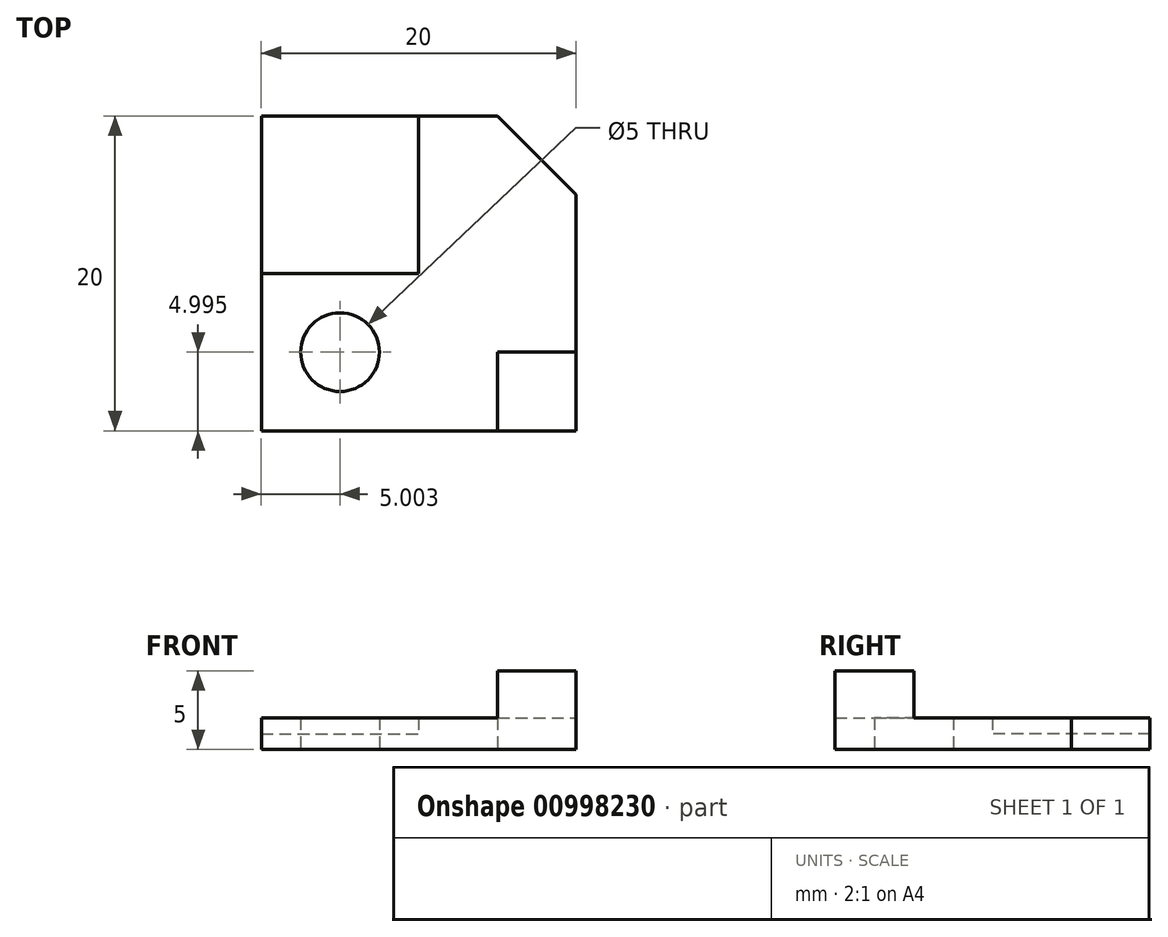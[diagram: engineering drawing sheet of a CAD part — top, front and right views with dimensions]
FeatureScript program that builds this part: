
annotation { "Feature Type Name" : "Feature", "Feature Type Description" : "" }
export const myFeature = defineFeature(function(context is Context, id is Id, definition is map)
    precondition{}
    {
        {
            var Q0;
            Q0=qCreatedBy(makeId("Top.planeOp"),FACE);
            var sketch = newSketch(context, id + "F0", { "sketchPlane" : qUnion([Q0])});
            skLineSegment(sketch, "E0.bottom", {"start": v(-62.42, 35.89) * mm, "end": v(-42.42, 35.89) * mm});
            skLineSegment(sketch, "E0.top", {"start": v(-62.42, 15.89) * mm, "end": v(-42.42, 15.89) * mm});
            skLineSegment(sketch, "E0.left", {"start": v(-62.42, 35.89) * mm, "end": v(-62.42, 15.89) * mm});
            skLineSegment(sketch, "E0.right", {"start": v(-42.42, 35.89) * mm, "end": v(-42.42, 15.89) * mm});
            skPoint(sketch, "E1.oppositeSnap0", {"position": v(-62.42, 25.89) * mm});
            skPoint(sketch, "E1.oppositeSnap1", {"position": v(-52.42, 35.89) * mm});
            skLineSegment(sketch, "E1.bottom", {"start": v(-62.42, 35.89) * mm, "end": v(-52.42, 35.89) * mm});
            skLineSegment(sketch, "E1.top", {"start": v(-62.42, 25.89) * mm, "end": v(-52.42, 25.89) * mm});
            skLineSegment(sketch, "E1.left", {"start": v(-62.42, 35.89) * mm, "end": v(-62.42, 25.89) * mm});
            skLineSegment(sketch, "E1.right", {"start": v(-52.42, 35.89) * mm, "end": v(-52.42, 25.89) * mm});
            skLineSegment(sketch, "E2.bottom", {"start": v(-42.42, 15.89) * mm, "end": v(-47.42, 15.89) * mm});
            skLineSegment(sketch, "E2.top", {"start": v(-42.42, 20.89) * mm, "end": v(-47.42, 20.89) * mm});
            skLineSegment(sketch, "E2.left", {"start": v(-42.42, 15.89) * mm, "end": v(-42.42, 20.89) * mm});
            skLineSegment(sketch, "E2.right", {"start": v(-47.42, 15.89) * mm, "end": v(-47.42, 20.89) * mm});
            skLineSegment(sketch, "E3", {"start": v(-52.42, 25.89) * mm, "end": v(-62.42, 15.89) * mm, "construction": true});
            skLineSegment(sketch, "E4", {"start": v(-62.42, 25.89) * mm, "end": v(-52.42, 15.89) * mm, "construction": true});
            skCircle(sketch, "E5", {"center": v(-57.42, 20.89) * mm, "radius": 2.5 * mm});
            skSolve(sketch);
        }
        {
            var Q0;
            {var subQ4=sQuery(id+"F0.wireOp",EDGE,"E1.top");Q0=makeQuery(id+"F0.imprint","IMPRINT",FACE,{"disambiguationData":[TD([[makeQuery(id+"F0.imprint","IMPRINT",EDGE,{"derivedFrom":subQ4}),1.0]])]});}
            extrude(context, id + "F1", {"entities" : qUnion([Q0]), "depth" : 1 * mm, "offsetDistance" : 25 * mm});
        }
        {
            var Q0;
            {var subQ3=sQuery(id+"F0.wireOp",EDGE,"E1.top");Q0=makeQuery(id+"F0.imprint","IMPRINT",FACE,{"disambiguationData":[TD([[makeQuery(id+"F0.imprint","IMPRINT",EDGE,{"derivedFrom":subQ3}),-1.0]])]});}
            extrude(context, id + "F2", {"entities" : qUnion([Q0]), "operationType" : NewBodyOperationType.ADD, "depth" : 2 * mm, "offsetDistance" : 25 * mm});
        }
        {
            var Q0;
            {var subQ4=sQuery(id+"F0.wireOp",EDGE,"E2.top");Q0=makeQuery(id+"F0.imprint","IMPRINT",FACE,{"disambiguationData":[TD([[makeQuery(id+"F0.imprint","IMPRINT",EDGE,{"derivedFrom":subQ4}),1.0]])]});}
            extrude(context, id + "F3", {"entities" : qUnion([Q0]), "operationType" : NewBodyOperationType.ADD, "depth" : 5 * mm, "offsetDistance" : 25 * mm});
        }
        {
            var Q0;
            Q0=makeQuery(id+"F2.opExtrude","SWEPT_EDGE",EDGE,{"disambiguationData":[OSD([sQuery(id+"F0.wireOp",EDGE,"E0.bottom"),sQuery(id+"F0.wireOp",EDGE,"E0.right")])]});
            chamfer(context, id + "F4", {"entities" : qUnion([Q0]), "width" : 5 * mm, "tangentPropagation" : true});
        }
    });
